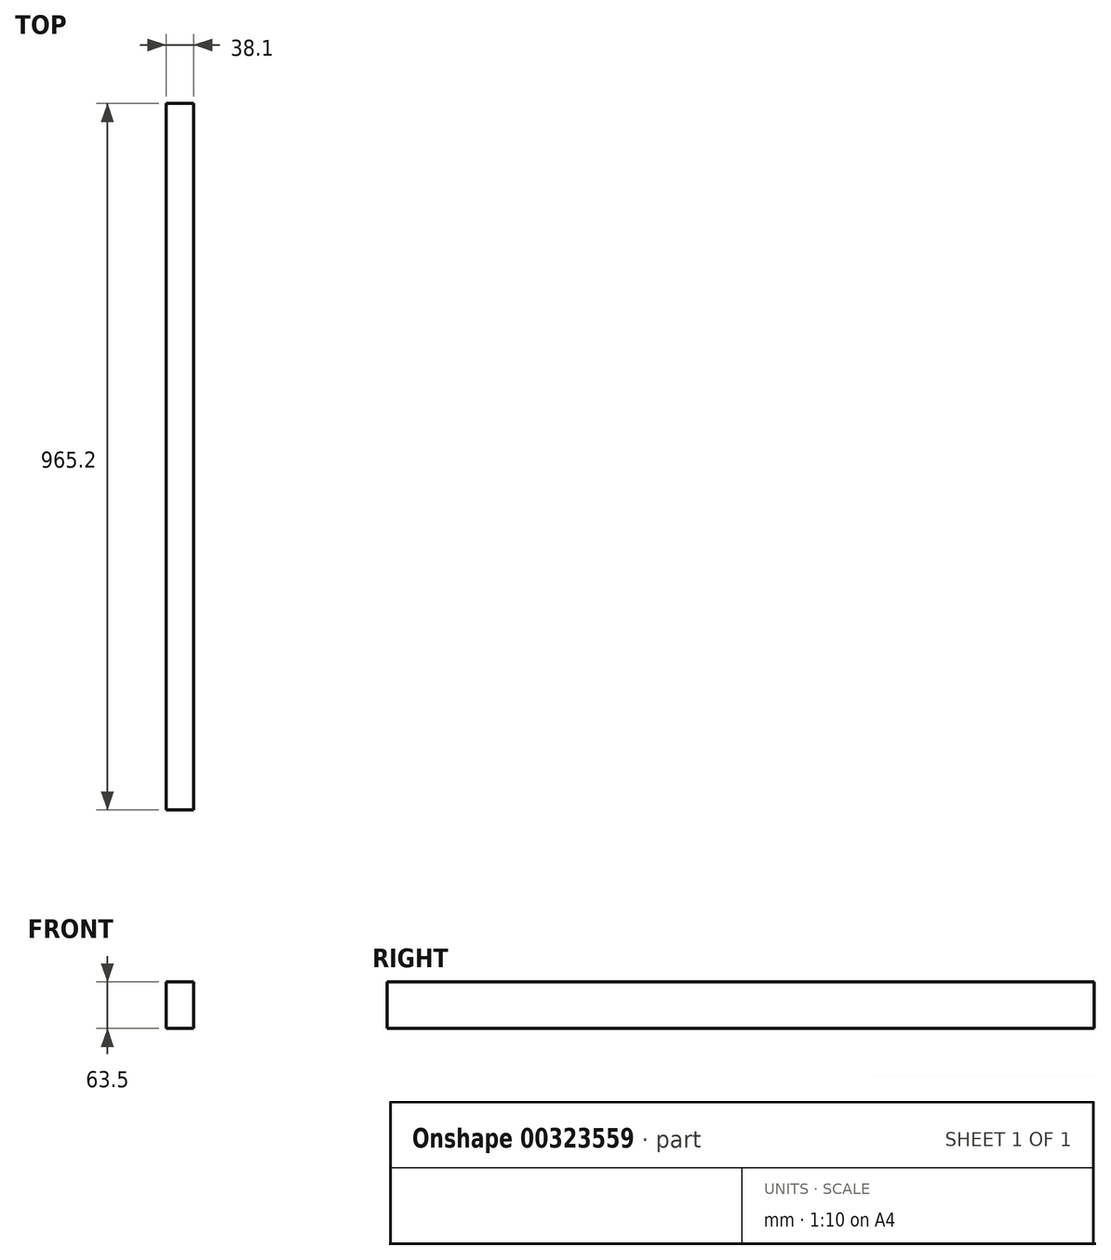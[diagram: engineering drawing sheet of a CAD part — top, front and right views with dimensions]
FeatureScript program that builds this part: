
annotation { "Feature Type Name" : "Feature", "Feature Type Description" : "" }
export const myFeature = defineFeature(function(context is Context, id is Id, definition is map)
    precondition{}
    {
        {
            var Q0;
            Q0=qCreatedBy(makeId("Right.planeOp"),FACE);
            var sketch = newSketch(context, id + "F0", { "sketchPlane" : qUnion([Q0])});
            skLineSegment(sketch, "E0.bottom", {"start": v(-482.6, 31.75) * mm, "end": v(482.6, 31.75) * mm});
            skLineSegment(sketch, "E0.top", {"start": v(-482.6, -31.75) * mm, "end": v(482.6, -31.75) * mm});
            skLineSegment(sketch, "E0.left", {"start": v(-482.6, 31.75) * mm, "end": v(-482.6, -31.75) * mm});
            skLineSegment(sketch, "E0.right", {"start": v(482.6, 31.75) * mm, "end": v(482.6, -31.75) * mm});
            skPoint(sketch, "E0.middle", {"position": v(0, 0) * mm});
            skSolve(sketch);
        }
        {
            var Q0;
            Q0=makeQuery(id+"F0.imprint","IMPRINT",FACE,{"disambiguationData":[TD([[makeQuery(id+"F0.imprint","IMPRINT",EDGE,{"derivedFrom":sQuery(id+"F0.wireOp",EDGE,"E0.bottom")}),-1.0]])]});
            extrude(context, id + "F1", {"entities" : qUnion([Q0]), "depth" : 38.1 * mm});
        }
        {
            var Q0;
            Q0=makeQuery(id+"F1.opExtrude","SWEPT_FACE",FACE,{"disambiguationData":[OSD([sQuery(id+"F0.wireOp",EDGE,"E0.bottom")])]});
            var sketch = newSketch(context, id + "F2", { "sketchPlane" : qUnion([Q0])});
            skPoint(sketch, "E1", {"position": v(19.05, 0) * mm});
            skSolve(sketch);
        }
        {
            var Q0;
            Q0=makeQuery(id+"F1.opExtrude","SWEPT_BODY",BODY,{"disambiguationData":[OSD([sQuery(id+"F0.wireOp",EDGE,"E0.bottom"),sQuery(id+"F0.wireOp",EDGE,"E0.top"),sQuery(id+"F0.wireOp",EDGE,"E0.left"),sQuery(id+"F0.wireOp",EDGE,"E0.right")])]});
            var Q1;
            Q1=sQuery(id+"F2.wireOp",VERTEX,"E1");
            var Q2;
            Q2=qCreatedBy(makeId("Origin.pointOp"),VERTEX);
            transform(context, id + "F3", {"entities" : qUnion([Q0]), "transformType" : TransformType.TRANSLATION_ENTITY, "oppositeDirectionEntity" : false, "transformLine" : qUnion([Q1, Q2]), "makeCopy" : false});
        }
        {
            var Q0;
            Q0=makeQuery(id+"F1.opExtrude","SWEPT_FACE",FACE,{"disambiguationData":[OSD([sQuery(id+"F0.wireOp",EDGE,"E0.bottom")])]});
            var sketch = newSketch(context, id + "F4", { "sketchPlane" : qUnion([Q0])});
            skPoint(sketch, "E2", {"position": v(0, 191.2) * mm});
            skSolve(sketch);
        }
        {
            var Q0;
            Q0=makeQuery(id+"F1.opExtrude","SWEPT_FACE",FACE,{"disambiguationData":[OSD([sQuery(id+"F0.wireOp",EDGE,"E0.right")])]});
            var sketch = newSketch(context, id + "F5", { "sketchPlane" : qUnion([Q0])});
            skLineSegment(sketch, "E3", {"start": v(0, -31.75) * mm, "end": v(-1231.9, -31.75) * mm});
            skPoint(sketch, "E3.startSnap0", {"position": v(-19.05, -31.75) * mm});
            skSolve(sketch);
        }
    });
